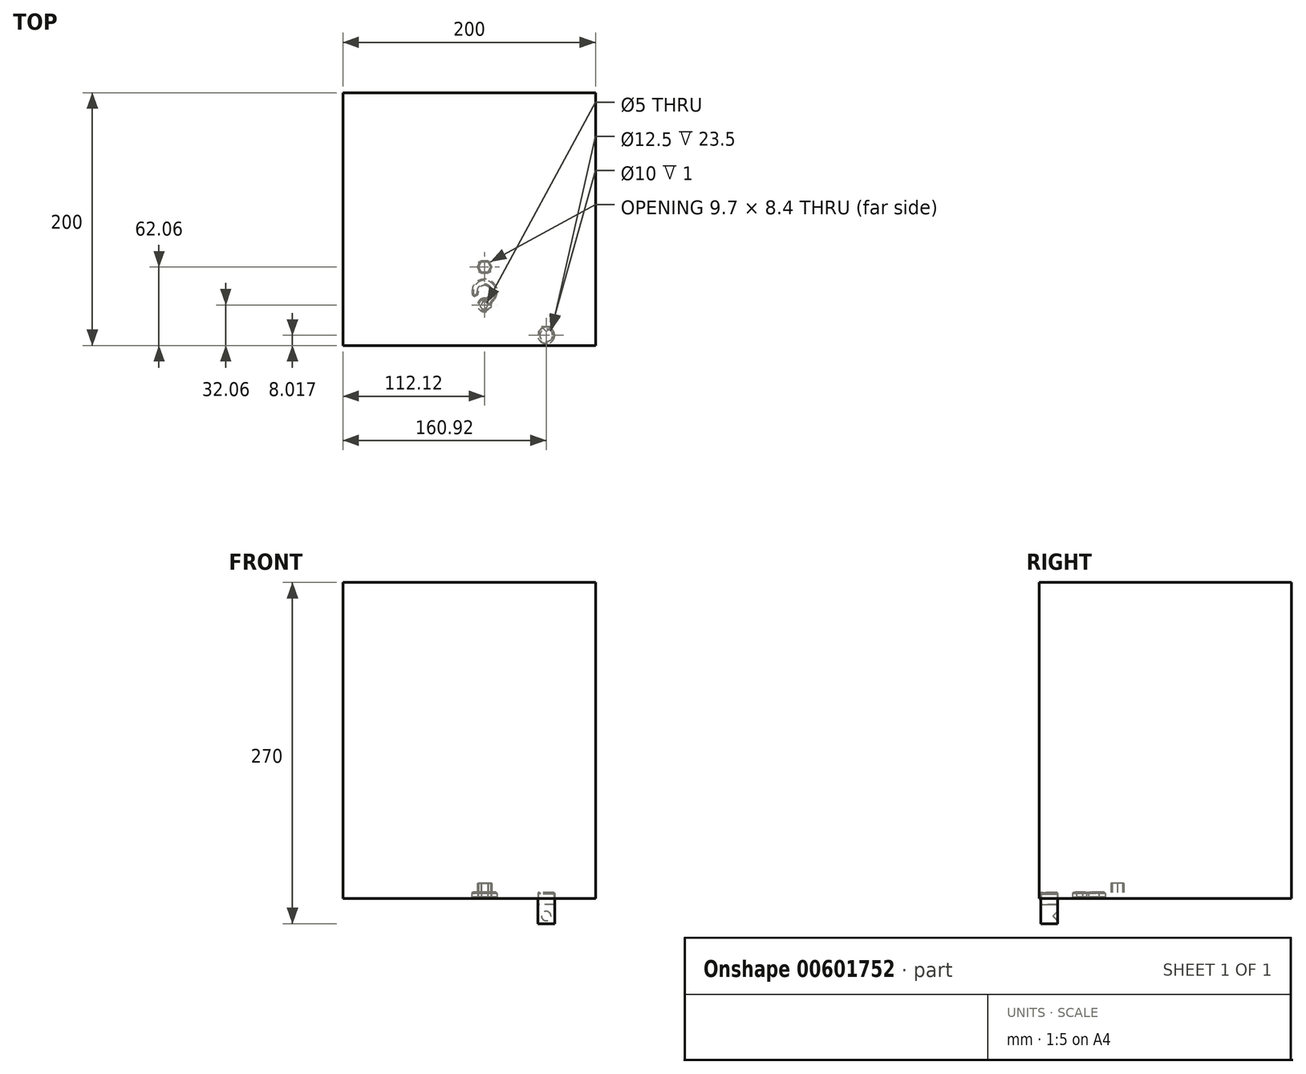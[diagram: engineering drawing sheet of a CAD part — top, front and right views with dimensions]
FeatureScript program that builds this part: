
annotation { "Feature Type Name" : "Feature", "Feature Type Description" : "" }
export const myFeature = defineFeature(function(context is Context, id is Id, definition is map)
    precondition{}
    {
        {
            var Q0;
            Q0=qCreatedBy(makeId("Top.planeOp"),FACE);
            var sketch = newSketch(context, id + "F0", { "sketchPlane" : qUnion([Q0])});
            skCircle(sketch, "E0", {"center": v(0, 0) * mm, "radius": 2.5 * mm});
            skCircle(sketch, "E1", {"center": v(0, 0) * mm, "radius": 5.5 * mm});
            skArc(sketch, "E2", {"start": v(0, 5.5) * mm, "mid": v(2.68, 14.72) * mm, "end": v(-4.52, 8.37) * mm});
            skArc(sketch, "E3", {"start": v(-5.15, 1.93) * mm, "mid": v(7.42, 17.2) * mm, "end": v(-9.05, 6.24) * mm});
            skLineSegment(sketch, "E4", {"start": v(0, 10.5) * mm, "end": v(-9.05, 6.24) * mm});
            skSolve(sketch);
        }
        {
            var Q0;
            {var subQ0=sQuery(id+"F0.wireOp",EDGE,"E2");Q0=makeQuery(id+"F0.imprint","IMPRINT",FACE,{"disambiguationData":[TD([[makeQuery(id+"F0.imprint","IMPRINT",EDGE,{"derivedFrom":subQ0}),-1.0]])]});}
            var Q1;
            {var subQ0=sQuery(id+"F0.wireOp",EDGE,"E1");var subQ1=makeQuery(id+"F0.imprint","INTERSECT",VERTEX,{"derivedFrom":[subQ0,sQuery(id+"F0.wireOp",EDGE,"E2")]});Q1=makeQuery(id+"F0.imprint","IMPRINT",FACE,{"disambiguationData":[TD([[makeQuery(id+"F0.imprint","IMPRINT",EDGE,{"disambiguationData":[TD([[subQ1,1.0]])],"derivedFrom":subQ0}),1.0]])]});}
            var Q2;
            {var subQ0=sQuery(id+"F0.wireOp",EDGE,"E0");Q2=makeQuery(id+"F0.imprint","IMPRINT",FACE,{"disambiguationData":[TD([[makeQuery(id+"F0.imprint","IMPRINT",EDGE,{"derivedFrom":subQ0}),-1.0]])]});}
            extrude(context, id + "F1", {"entities" : qUnion([Q0, Q1, Q2]), "depth" : 5 * mm, "offsetDistance" : 25 * mm});
        }
        {
            var Q0;
            Q0=makeQuery(id+"F1.opExtrude","SWEPT_EDGE",EDGE,{"disambiguationData":[OSD([sQuery(id+"F0.wireOp",EDGE,"E2"),sQuery(id+"F0.wireOp",EDGE,"E4")])]});
            var Q1;
            Q1=makeQuery(id+"F1.opExtrude","SWEPT_EDGE",EDGE,{"disambiguationData":[OSD([sQuery(id+"F0.wireOp",EDGE,"E3"),sQuery(id+"F0.wireOp",EDGE,"E4")])]});
            var Q2;
            Q2=makeQuery(id+"F1.opExtrude","SWEPT_EDGE",EDGE,{"disambiguationData":[OSD([sQuery(id+"F0.wireOp",EDGE,"E1"),sQuery(id+"F0.wireOp",EDGE,"E3")])]});
            fillet(context, id + "F2", {"entities" : qUnion([Q0, Q1, Q2]), "radius" : 2 * mm, "tangentPropagation" : true, "allowEdgeOverflow" : false});
        }
        {
            var Q0;
            Q0=makeQuery(id+"F1.opExtrude","CAP_EDGE",EDGE,{"disambiguationData":[OSD([sQuery(id+"F0.wireOp",EDGE,"E1")])],"isStart":false});
            var Q1;
            Q1=makeQuery(id+"F1.opExtrude","CAP_EDGE",EDGE,{"disambiguationData":[OSD([sQuery(id+"F0.wireOp",EDGE,"E3")])],"isStart":true});
            var Q2;
            Q2=makeQuery(id+"F1.opExtrude","CAP_EDGE",EDGE,{"disambiguationData":[OSD([sQuery(id+"F0.wireOp",EDGE,"E0")])],"isStart":false});
            var Q3;
            Q3=makeQuery(id+"F1.opExtrude","CAP_EDGE",EDGE,{"disambiguationData":[OSD([sQuery(id+"F0.wireOp",EDGE,"E0")])],"isStart":true});
            chamfer(context, id + "F3", {"entities" : qUnion([Q0, Q1, Q2, Q3]), "width" : 1 * mm, "tangentPropagation" : true});
        }
        {
            var Q0;
            Q0=qCreatedBy(makeId("Top.planeOp"),FACE);
            var sketch = newSketch(context, id + "F4", { "sketchPlane" : qUnion([Q0])});
            skCircle(sketch, "E5.cCircle", {"center": v(0, 30) * mm, "radius": 4.2 * mm, "construction": true});
            skLineSegment(sketch, "E5.0", {"start": v(4.85, 30) * mm, "end": v(2.42, 25.8) * mm});
            skLineSegment(sketch, "E5.1", {"start": v(2.42, 25.8) * mm, "end": v(-2.42, 25.8) * mm});
            skLineSegment(sketch, "E5.2", {"start": v(-2.42, 25.8) * mm, "end": v(-4.85, 30) * mm});
            skLineSegment(sketch, "E5.3", {"start": v(-4.85, 30) * mm, "end": v(-2.42, 34.2) * mm});
            skLineSegment(sketch, "E5.4", {"start": v(-2.42, 34.2) * mm, "end": v(2.42, 34.2) * mm});
            skLineSegment(sketch, "E5.5", {"start": v(2.42, 34.2) * mm, "end": v(4.85, 30) * mm});
            skPoint(sketch, "E5.0.midPoint", {"position": v(3.64, 27.9) * mm});
            skCircle(sketch, "E6.cCircle", {"center": v(0, 30) * mm, "radius": 5 * mm, "construction": true});
            skLineSegment(sketch, "E6.0", {"start": v(5.77, 30) * mm, "end": v(2.89, 25) * mm});
            skLineSegment(sketch, "E6.1", {"start": v(2.89, 25) * mm, "end": v(-2.89, 25) * mm});
            skLineSegment(sketch, "E6.2", {"start": v(-2.89, 25) * mm, "end": v(-5.77, 30) * mm});
            skLineSegment(sketch, "E6.3", {"start": v(-5.77, 30) * mm, "end": v(-2.89, 35) * mm});
            skLineSegment(sketch, "E6.4", {"start": v(-2.89, 35) * mm, "end": v(2.89, 35) * mm});
            skLineSegment(sketch, "E6.5", {"start": v(2.89, 35) * mm, "end": v(5.77, 30) * mm});
            skPoint(sketch, "E6.0.midPoint", {"position": v(4.33, 27.5) * mm});
            skSolve(sketch);
        }
        {
            var Q0;
            Q0=makeQuery(id+"F4.imprint","IMPRINT",FACE,{"disambiguationData":[TD([[makeQuery(id+"F4.imprint","IMPRINT",EDGE,{"derivedFrom":sQuery(id+"F4.wireOp",EDGE,"E5.0")}),1.0]])]});
            extrude(context, id + "F5", {"entities" : qUnion([Q0]), "depth" : 12 * mm, "offsetDistance" : 25 * mm});
        }
        {
            var Q0;
            Q0=qCreatedBy(makeId("Top.planeOp"),FACE);
            var sketch = newSketch(context, id + "F6", { "sketchPlane" : qUnion([Q0])});
            skCircle(sketch, "E7", {"center": v(48.8, -24.04) * mm, "radius": 6.65 * mm});
            skCircle(sketch, "E8", {"center": v(48.8, -24.04) * mm, "radius": 6.25 * mm});
            skSolve(sketch);
        }
        {
            var Q0;
            Q0=makeQuery(id+"F6.imprint","IMPRINT",FACE,{"disambiguationData":[TD([[makeQuery(id+"F6.imprint","IMPRINT",EDGE,{"derivedFrom":sQuery(id+"F6.wireOp",EDGE,"E7")}),1.0]])]});
            extrude(context, id + "F7", {"entities" : qUnion([Q0]), "depth" : 3.5 * mm, "offsetDistance" : 25 * mm});
        }
        {
            var Q0;
            Q0=makeQuery(id+"F7.opExtrude","CAP_FACE",FACE,{"disambiguationData":[OSD([sQuery(id+"F6.wireOp",EDGE,"E7"),sQuery(id+"F6.wireOp",EDGE,"E8")])],"isStart":false});
            var sketch = newSketch(context, id + "F8", { "sketchPlane" : qUnion([Q0])});
            skCircle(sketch, "E9", {"center": v(48.8, -24.04) * mm, "radius": 5 * mm});
            skCircle(sketch, "E10.0", {"center": v(48.8, -24.04) * mm, "radius": 6.65 * mm});
            skSolve(sketch);
        }
        {
            var Q0;
            Q0=makeQuery(id+"F8.imprint","IMPRINT",FACE,{"disambiguationData":[TD([[makeQuery(id+"F8.imprint","IMPRINT",EDGE,{"derivedFrom":sQuery(id+"F8.wireOp",EDGE,"E9")}),-1.0]])]});
            var Q1;
            Q1=makeQuery(id+"F8.imprint","IMPRINT",FACE,{"disambiguationData":[TD([[makeQuery(id+"F8.imprint","IMPRINT",EDGE,{"derivedFrom":sQuery(id+"F8.wireOp",EDGE,"E10.0")}),1.0]])]});
            extrude(context, id + "F9", {"entities" : qUnion([Q0, Q1]), "operationType" : NewBodyOperationType.ADD, "depth" : 1 * mm, "offsetDistance" : 25 * mm});
        }
        {
            var Q0;
            Q0=makeQuery(id+"F7.opExtrude","CAP_FACE",FACE,{"disambiguationData":[OSD([sQuery(id+"F6.wireOp",EDGE,"E7"),sQuery(id+"F6.wireOp",EDGE,"E8")])],"isStart":true});
            extrude(context, id + "F10", {"entities" : qUnion([Q0]), "operationType" : NewBodyOperationType.ADD, "depth" : 20 * mm, "offsetDistance" : 25 * mm});
        }
        {
            var Q0;
            Q0=makeQuery(id+"F10.opExtrude","CAP_FACE",FACE,{"disambiguationData":[OSD([sQuery(id+"F6.wireOp",EDGE,"E7"),sQuery(id+"F6.wireOp",EDGE,"E8")])],"isStart":false});
            var sketch = newSketch(context, id + "F11", { "sketchPlane" : qUnion([Q0])});
            skCircle(sketch, "E11.0", {"center": v(48.8, 24.04) * mm, "radius": 6.25 * mm});
            skSolve(sketch);
        }
        {
            var Q0;
            Q0 = qSketchRegion(id + "F11", true);
            extrude(context, id + "F12", {"entities" : qUnion([Q0]), "oppositeDirection" : true, "depth" : 15 * mm, "offsetDistance" : 25 * mm});
        }
        {
            var Q0;
            Q0=qCreatedBy(makeId("Front.planeOp"),FACE);
            var sketch = newSketch(context, id + "F13", { "sketchPlane" : qUnion([Q0])});
            skLineSegment(sketch, "E12", {"start": v(42.15, -20) * mm, "end": v(42.15, 4.5) * mm});
            skLineSegment(sketch, "E13", {"start": v(55.45, 4.5) * mm, "end": v(55.45, -20) * mm});
            skLineSegment(sketch, "E14.0", {"start": v(42.15, -20) * mm, "end": v(55.45, -20) * mm});
            skLineSegment(sketch, "E15.0", {"start": v(42.15, 4.5) * mm, "end": v(55.45, 4.5) * mm});
            skCircle(sketch, "E16", {"center": v(48.8, -14) * mm, "radius": 1.55 * mm});
            skPoint(sketch, "E16.centerSnap0", {"position": v(48.8, -20) * mm});
            skSolve(sketch);
        }
        {
            var Q0;
            Q0=makeQuery(id+"F10.opExtrude","CAP_FACE",FACE,{"disambiguationData":[OSD([sQuery(id+"F6.wireOp",EDGE,"E7"),sQuery(id+"F6.wireOp",EDGE,"E8")])],"isStart":false});
            var sketch = newSketch(context, id + "F14", { "sketchPlane" : qUnion([Q0])});
            skPoint(sketch, "E17", {"position": v(48.8, 17.4) * mm});
            skLineSegment(sketch, "E18", {"start": v(0, 17.4) * mm, "end": v(60.07, 17.4) * mm});
            skSolve(sketch);
        }
        {
            var Q0;
            Q0=qCreatedBy(makeId("Front.planeOp"),FACE);
            var Q1;
            Q1=sQuery(id+"F14.wireOp",VERTEX,"E17");
            cPlane(context, id + "F15", {"entities" : qUnion([Q0, Q1]), "cplaneType" : CPlaneType.PLANE_POINT, "offset" : 25 * mm, "width" : 150 * mm, "height" : 150 * mm});
        }
        {
            var Q0;
            Q0=qCreatedBy(id+"F15.planeOp",FACE);
            var sketch = newSketch(context, id + "F16", { "sketchPlane" : qUnion([Q0])});
            skCircle(sketch, "E19.0", {"center": v(48.8, -14) * mm, "radius": 1.55 * mm});
            skCircle(sketch, "E20", {"center": v(48.8, -14) * mm, "radius": 3.75 * mm});
            skSolve(sketch);
        }
        {
            var Q0;
            Q0=makeQuery(id+"F16.imprint","IMPRINT",FACE,{"disambiguationData":[TD([[makeQuery(id+"F16.imprint","IMPRINT",EDGE,{"derivedFrom":sQuery(id+"F16.wireOp",EDGE,"E19.0")}),-1.0]])]});
            var Q1;
            Q1=makeQuery(id+"F16.imprint","IMPRINT",FACE,{"disambiguationData":[TD([[makeQuery(id+"F16.imprint","IMPRINT",EDGE,{"derivedFrom":sQuery(id+"F16.wireOp",EDGE,"E19.0")}),1.0]])]});
            extrude(context, id + "F17", {"entities" : qUnion([Q0, Q1]), "depth" : 25 * mm, "offsetDistance" : 25 * mm, "hasDraft" : true, "draftAngle" : 45 * degree, "draftPullDirection" : true});
        }
        {
            var Q0;
            Q0=makeQuery(id+"F9.opExtrude","CAP_EDGE",EDGE,{"disambiguationData":[OSD([sQuery(id+"F8.wireOp",EDGE,"E10.0")])],"isStart":false});
            chamfer(context, id + "F18", {"entities" : qUnion([Q0]), "width" : 0.4 * mm, "tangentPropagation" : true});
        }
        {
            var Q0;
            Q0=qCreatedBy(makeId("Top.planeOp"),FACE);
            var sketch = newSketch(context, id + "F19", { "sketchPlane" : qUnion([Q0])});
            skLineSegment(sketch, "E21.bottom", {"start": v(-112.12, 167.94) * mm, "end": v(87.88, 167.94) * mm});
            skLineSegment(sketch, "E21.top", {"start": v(-112.12, -32.06) * mm, "end": v(87.88, -32.06) * mm});
            skLineSegment(sketch, "E21.left", {"start": v(-112.12, 167.94) * mm, "end": v(-112.12, -32.06) * mm});
            skLineSegment(sketch, "E21.right", {"start": v(87.88, 167.94) * mm, "end": v(87.88, -32.06) * mm});
            skSolve(sketch);
        }
        {
            var Q0;
            Q0 = qSketchRegion(id + "F19", true);
            extrude(context, id + "F20", {"entities" : qUnion([Q0]), "depth" : 250 * mm, "offsetDistance" : 25 * mm});
        }
    });
